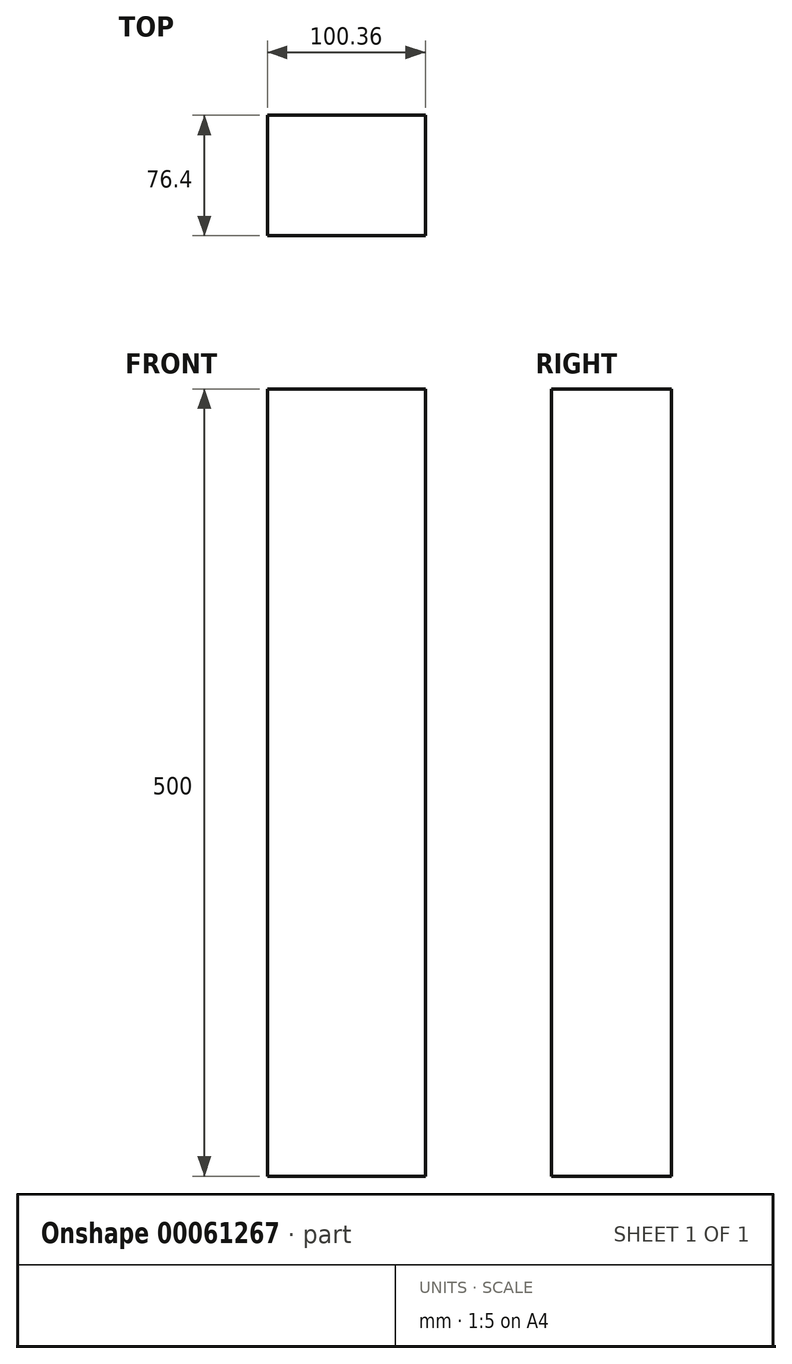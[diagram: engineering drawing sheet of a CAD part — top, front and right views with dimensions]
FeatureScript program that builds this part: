
annotation { "Feature Type Name" : "Feature", "Feature Type Description" : "" }
export const myFeature = defineFeature(function(context is Context, id is Id, definition is map)
    precondition{}
    {
        {
            var Q0;
            Q0=qCreatedBy(makeId("Top.planeOp"),FACE);
            var sketch = newSketch(context, id + "F0", { "sketchPlane" : qUnion([Q0])});
            skLineSegment(sketch, "E0.rect.bottom", {"start": v(-50.18, -38.2) * mm, "end": v(50.18, -38.2) * mm});
            skLineSegment(sketch, "E0.rect.top", {"start": v(-50.18, 38.2) * mm, "end": v(50.18, 38.2) * mm});
            skLineSegment(sketch, "E0.rect.left", {"start": v(-50.18, -38.2) * mm, "end": v(-50.18, 38.2) * mm});
            skLineSegment(sketch, "E0.rect.right", {"start": v(50.18, -38.2) * mm, "end": v(50.18, 38.2) * mm});
            skPoint(sketch, "E0.rect.middle", {"position": v(0, 0) * mm});
            skSolve(sketch);
        }
        {
            var Q0;
            Q0=makeQuery(id+"F0.imprint","IMPRINT",FACE,{"disambiguationData":[TD([[makeQuery(id+"F0.imprint","IMPRINT",EDGE,{"derivedFrom":sQuery(id+"F0.wireOp",EDGE,"E0.rect.bottom")}),1.0]])]});
            extrude(context, id + "F1", {"entities" : qUnion([Q0]), "depth" : 500 * mm});
        }
    });
